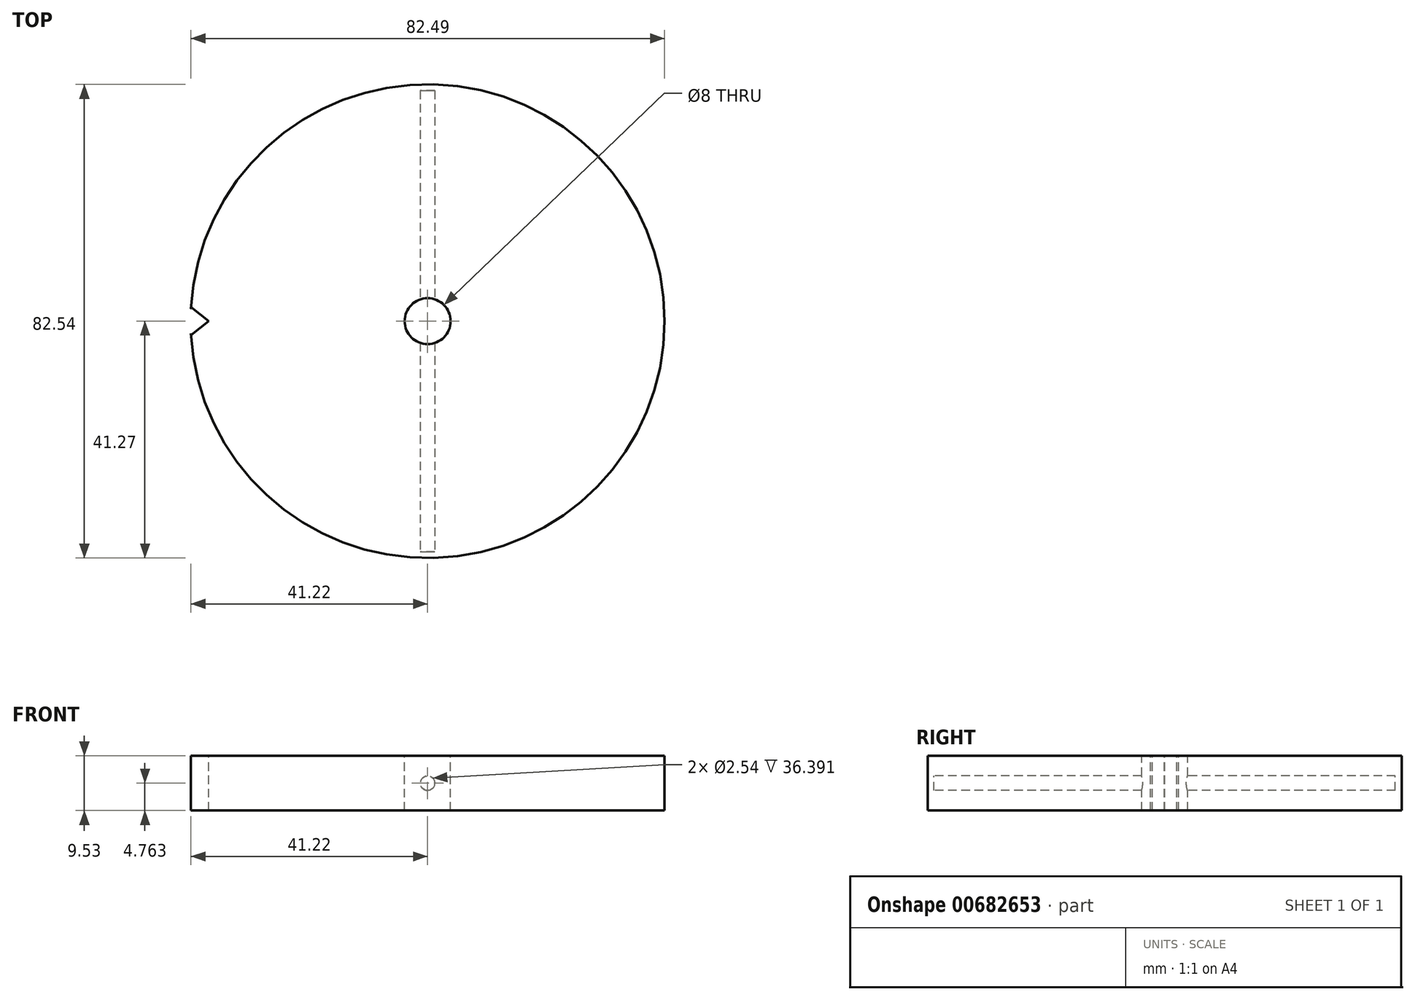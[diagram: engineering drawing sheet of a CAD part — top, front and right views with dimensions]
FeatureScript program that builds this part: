
annotation { "Feature Type Name" : "Feature", "Feature Type Description" : "" }
export const myFeature = defineFeature(function(context is Context, id is Id, definition is map)
    precondition{}
    {
        {
            var Q0;
            Q0=qCreatedBy(makeId("Top.planeOp"),FACE);
            var sketch = newSketch(context, id + "F0", { "sketchPlane" : qUnion([Q0])});
            skCircle(sketch, "E0", {"center": v(0, 0) * mm, "radius": 41.27 * mm});
            skSolve(sketch);
        }
        {
            var Q0;
            Q0 = qSketchRegion(id + "F0", true);
            extrude(context, id + "F1", {"entities" : qUnion([Q0]), "depth" : 9.52 * mm, "offsetDistance" : 25.4 * mm});
        }
        {
            var Q0;
            Q0=makeQuery(id+"F1.opExtrude","CAP_FACE",FACE,{"disambiguationData":[OSD([sQuery(id+"F0.wireOp",EDGE,"E0")])],"isStart":false});
            var sketch = newSketch(context, id + "F2", { "sketchPlane" : qUnion([Q0])});
            skCircle(sketch, "E1", {"center": v(0, 0) * mm, "radius": 38.1 * mm});
            skArc(sketch, "E2", {"start": v(3.17, 41.15) * mm, "mid": v(0, 38.1) * mm, "end": v(-3.17, 41.15) * mm});
            skLineSegment(sketch, "E3", {"start": v(-38.08, 0) * mm, "end": v(-41.19, 2.42) * mm});
            skLineSegment(sketch, "E4.MirrorCS", {"start": v(-38.08, 0) * mm, "end": v(-41.19, -2.42) * mm});
            skArc(sketch, "E5", {"start": v(-41.19, 2.42) * mm, "mid": v(-41.34, 0) * mm, "end": v(-41.19, -2.42) * mm});
            skSolve(sketch);
        }
        {
            var Q0;
            {var subQ1=sQuery(id+"F2.wireOp",EDGE,"E3");var subQ7=sQuery(id+"F2.wireOp",EDGE,"E1");var subQ9=makeQuery(id+"F2.imprint","INTERSECT",VERTEX,{"derivedFrom":[subQ7,subQ1]});Q0=makeQuery(id+"F2.imprint","IMPRINT",FACE,{"disambiguationData":[TD([[makeQuery(id+"F2.imprint","IMPRINT",EDGE,{"disambiguationData":[TD([[subQ9,-1.0]])],"derivedFrom":subQ7}),-1.0]])]});}
            var Q1;
            Q1=sQuery(id+"F2.wireOp",EDGE,"E3");
            var Q2;
            Q2=sQuery(id+"F2.wireOp",EDGE,"E4.MirrorCS");
            extrude(context, id + "F3", {"entities" : qUnion([Q0]), "operationType" : NewBodyOperationType.REMOVE, "flatOperationType" : FlatOperationType.REMOVE, "surfaceEntities" : qUnion([Q1, Q2]), "oppositeDirection" : true, "depth" : 25.4 * mm, "offsetDistance" : 25.4 * mm, "domain" : OperationDomain.MODEL});
        }
        {
            var Q0;
            {var subQ0=sQuery(id+"F2.wireOp",EDGE,"E1");var subQ180=makeQuery(id+"F3.boolean.opBoolean","COPY",FACE,{"derivedFrom":makeQuery(id+"F3.opExtrude","SWEPT_FACE",FACE,{"disambiguationData":[OSD([subQ0])]})});var subQ327=sQuery(id+"F0.wireOp",EDGE,"E0");Q0=makeQuery(id+"FR4VeuBJqVnm1tW_1.55.F3.boolean.opBoolean","SPLIT",FACE,{"disambiguationData":[TD([subQ180])],"derivedFrom":makeQuery(id+"FR4VeuBJqVnm1tW_1.54.F3.boolean.opBoolean","SPLIT",FACE,{"disambiguationData":[TD([subQ180])],"derivedFrom":makeQuery(id+"FR4VeuBJqVnm1tW_1.53.F3.boolean.opBoolean","SPLIT",FACE,{"disambiguationData":[TD([subQ180])],"derivedFrom":makeQuery(id+"FR4VeuBJqVnm1tW_1.52.F3.boolean.opBoolean","SPLIT",FACE,{"disambiguationData":[TD([subQ180])],"derivedFrom":makeQuery(id+"FR4VeuBJqVnm1tW_1.51.F3.boolean.opBoolean","SPLIT",FACE,{"disambiguationData":[TD([subQ180])],"derivedFrom":makeQuery(id+"FR4VeuBJqVnm1tW_1.50.F3.boolean.opBoolean","SPLIT",FACE,{"disambiguationData":[TD([subQ180])],"derivedFrom":makeQuery(id+"FR4VeuBJqVnm1tW_1.49.F3.boolean.opBoolean","SPLIT",FACE,{"disambiguationData":[TD([subQ180])],"derivedFrom":makeQuery(id+"FR4VeuBJqVnm1tW_1.48.F3.boolean.opBoolean","SPLIT",FACE,{"disambiguationData":[TD([subQ180])],"derivedFrom":makeQuery(id+"FR4VeuBJqVnm1tW_1.47.F3.boolean.opBoolean","SPLIT",FACE,{"disambiguationData":[TD([subQ180])],"derivedFrom":makeQuery(id+"FR4VeuBJqVnm1tW_1.46.F3.boolean.opBoolean","SPLIT",FACE,{"disambiguationData":[TD([subQ180])],"derivedFrom":makeQuery(id+"FR4VeuBJqVnm1tW_1.45.F3.boolean.opBoolean","SPLIT",FACE,{"disambiguationData":[TD([subQ180])],"derivedFrom":makeQuery(id+"FR4VeuBJqVnm1tW_1.44.F3.boolean.opBoolean","SPLIT",FACE,{"disambiguationData":[TD([subQ180])],"derivedFrom":makeQuery(id+"FR4VeuBJqVnm1tW_1.43.F3.boolean.opBoolean","SPLIT",FACE,{"disambiguationData":[TD([subQ180])],"derivedFrom":makeQuery(id+"FR4VeuBJqVnm1tW_1.42.F3.boolean.opBoolean","SPLIT",FACE,{"disambiguationData":[TD([subQ180])],"derivedFrom":makeQuery(id+"FR4VeuBJqVnm1tW_1.41.F3.boolean.opBoolean","SPLIT",FACE,{"disambiguationData":[TD([subQ180])],"derivedFrom":makeQuery(id+"FR4VeuBJqVnm1tW_1.40.F3.boolean.opBoolean","SPLIT",FACE,{"disambiguationData":[TD([subQ180])],"derivedFrom":makeQuery(id+"FR4VeuBJqVnm1tW_1.39.F3.boolean.opBoolean","SPLIT",FACE,{"disambiguationData":[TD([subQ180])],"derivedFrom":makeQuery(id+"FR4VeuBJqVnm1tW_1.38.F3.boolean.opBoolean","SPLIT",FACE,{"disambiguationData":[TD([subQ180])],"derivedFrom":makeQuery(id+"FR4VeuBJqVnm1tW_1.37.F3.boolean.opBoolean","SPLIT",FACE,{"disambiguationData":[TD([subQ180])],"derivedFrom":makeQuery(id+"FR4VeuBJqVnm1tW_1.36.F3.boolean.opBoolean","SPLIT",FACE,{"disambiguationData":[TD([subQ180])],"derivedFrom":makeQuery(id+"FR4VeuBJqVnm1tW_1.35.F3.boolean.opBoolean","SPLIT",FACE,{"disambiguationData":[TD([subQ180])],"derivedFrom":makeQuery(id+"FR4VeuBJqVnm1tW_1.34.F3.boolean.opBoolean","SPLIT",FACE,{"disambiguationData":[TD([subQ180])],"derivedFrom":makeQuery(id+"FR4VeuBJqVnm1tW_1.33.F3.boolean.opBoolean","SPLIT",FACE,{"disambiguationData":[TD([subQ180])],"derivedFrom":makeQuery(id+"FR4VeuBJqVnm1tW_1.32.F3.boolean.opBoolean","SPLIT",FACE,{"disambiguationData":[TD([subQ180])],"derivedFrom":makeQuery(id+"FR4VeuBJqVnm1tW_1.31.F3.boolean.opBoolean","SPLIT",FACE,{"disambiguationData":[TD([subQ180])],"derivedFrom":makeQuery(id+"FR4VeuBJqVnm1tW_1.30.F3.boolean.opBoolean","SPLIT",FACE,{"disambiguationData":[TD([subQ180])],"derivedFrom":makeQuery(id+"FR4VeuBJqVnm1tW_1.29.F3.boolean.opBoolean","SPLIT",FACE,{"disambiguationData":[TD([subQ180])],"derivedFrom":makeQuery(id+"FR4VeuBJqVnm1tW_1.28.F3.boolean.opBoolean","SPLIT",FACE,{"disambiguationData":[TD([subQ180])],"derivedFrom":makeQuery(id+"FR4VeuBJqVnm1tW_1.27.F3.boolean.opBoolean","SPLIT",FACE,{"disambiguationData":[TD([subQ180])],"derivedFrom":makeQuery(id+"FR4VeuBJqVnm1tW_1.26.F3.boolean.opBoolean","SPLIT",FACE,{"disambiguationData":[TD([subQ180])],"derivedFrom":makeQuery(id+"FR4VeuBJqVnm1tW_1.25.F3.boolean.opBoolean","SPLIT",FACE,{"disambiguationData":[TD([subQ180])],"derivedFrom":makeQuery(id+"FR4VeuBJqVnm1tW_1.24.F3.boolean.opBoolean","SPLIT",FACE,{"disambiguationData":[TD([subQ180])],"derivedFrom":makeQuery(id+"FR4VeuBJqVnm1tW_1.23.F3.boolean.opBoolean","SPLIT",FACE,{"disambiguationData":[TD([subQ180])],"derivedFrom":makeQuery(id+"FR4VeuBJqVnm1tW_1.22.F3.boolean.opBoolean","SPLIT",FACE,{"disambiguationData":[TD([subQ180])],"derivedFrom":makeQuery(id+"FR4VeuBJqVnm1tW_1.21.F3.boolean.opBoolean","SPLIT",FACE,{"disambiguationData":[TD([subQ180])],"derivedFrom":makeQuery(id+"FR4VeuBJqVnm1tW_1.20.F3.boolean.opBoolean","SPLIT",FACE,{"disambiguationData":[TD([subQ180])],"derivedFrom":makeQuery(id+"FR4VeuBJqVnm1tW_1.19.F3.boolean.opBoolean","SPLIT",FACE,{"disambiguationData":[TD([subQ180])],"derivedFrom":makeQuery(id+"FR4VeuBJqVnm1tW_1.18.F3.boolean.opBoolean","SPLIT",FACE,{"disambiguationData":[TD([subQ180])],"derivedFrom":makeQuery(id+"FR4VeuBJqVnm1tW_1.17.F3.boolean.opBoolean","SPLIT",FACE,{"disambiguationData":[TD([subQ180])],"derivedFrom":makeQuery(id+"FR4VeuBJqVnm1tW_1.16.F3.boolean.opBoolean","SPLIT",FACE,{"disambiguationData":[TD([subQ180])],"derivedFrom":makeQuery(id+"FR4VeuBJqVnm1tW_1.15.F3.boolean.opBoolean","SPLIT",FACE,{"disambiguationData":[TD([subQ180])],"derivedFrom":makeQuery(id+"FR4VeuBJqVnm1tW_1.14.F3.boolean.opBoolean","SPLIT",FACE,{"disambiguationData":[TD([subQ180])],"derivedFrom":makeQuery(id+"FR4VeuBJqVnm1tW_1.13.F3.boolean.opBoolean","SPLIT",FACE,{"disambiguationData":[TD([subQ180])],"derivedFrom":makeQuery(id+"FR4VeuBJqVnm1tW_1.12.F3.boolean.opBoolean","SPLIT",FACE,{"disambiguationData":[TD([subQ180])],"derivedFrom":makeQuery(id+"FR4VeuBJqVnm1tW_1.11.F3.boolean.opBoolean","SPLIT",FACE,{"disambiguationData":[TD([subQ180])],"derivedFrom":makeQuery(id+"FR4VeuBJqVnm1tW_1.10.F3.boolean.opBoolean","SPLIT",FACE,{"disambiguationData":[TD([subQ180])],"derivedFrom":makeQuery(id+"FR4VeuBJqVnm1tW_1.9.F3.boolean.opBoolean","SPLIT",FACE,{"disambiguationData":[TD([subQ180])],"derivedFrom":makeQuery(id+"FR4VeuBJqVnm1tW_1.8.F3.boolean.opBoolean","SPLIT",FACE,{"disambiguationData":[TD([subQ180])],"derivedFrom":makeQuery(id+"FR4VeuBJqVnm1tW_1.7.F3.boolean.opBoolean","SPLIT",FACE,{"disambiguationData":[TD([subQ180])],"derivedFrom":makeQuery(id+"FR4VeuBJqVnm1tW_1.6.F3.boolean.opBoolean","SPLIT",FACE,{"disambiguationData":[TD([subQ180])],"derivedFrom":makeQuery(id+"FR4VeuBJqVnm1tW_1.5.F3.boolean.opBoolean","SPLIT",FACE,{"disambiguationData":[TD([subQ180])],"derivedFrom":makeQuery(id+"FR4VeuBJqVnm1tW_1.4.F3.boolean.opBoolean","SPLIT",FACE,{"disambiguationData":[TD([subQ180])],"derivedFrom":makeQuery(id+"FR4VeuBJqVnm1tW_1.3.F3.boolean.opBoolean","SPLIT",FACE,{"disambiguationData":[TD([subQ180])],"derivedFrom":makeQuery(id+"FR4VeuBJqVnm1tW_1.2.F3.boolean.opBoolean","SPLIT",FACE,{"disambiguationData":[TD([subQ180])],"derivedFrom":makeQuery(id+"FR4VeuBJqVnm1tW_1.1.F3.boolean.opBoolean","SPLIT",FACE,{"disambiguationData":[TD([subQ180])],"derivedFrom":makeQuery(id+"F1.opExtrude","CAP_FACE",FACE,{"disambiguationData":[OSD([subQ327])],"isStart":false})})})})})})})})})})})})})})})})})})})})})})})})})})})})})})})})})})})})})})})})})})})})})})})})})})})})})})})});}
            var sketch = newSketch(context, id + "F4", { "sketchPlane" : qUnion([Q0])});
            skCircle(sketch, "E6", {"center": v(0, 0) * mm, "radius": 4 * mm});
            skSolve(sketch);
        }
        {
            var Q0;
            Q0 = qSketchRegion(id + "F4", true);
            extrude(context, id + "F5", {"entities" : qUnion([Q0]), "operationType" : NewBodyOperationType.REMOVE, "flatOperationType" : FlatOperationType.REMOVE, "oppositeDirection" : true, "depth" : 25.4 * mm, "offsetDistance" : 25.4 * mm, "domain" : OperationDomain.MODEL});
        }
        {
            var Q0;
            Q0=qCreatedBy(makeId("Front.planeOp"),FACE);
            var sketch = newSketch(context, id + "F6", { "sketchPlane" : qUnion([Q0])});
            skLineSegment(sketch, "E7", {"start": v(0, 0) * mm, "end": v(0, 4.76) * mm});
            skCircle(sketch, "E8", {"center": v(0, 4.76) * mm, "radius": 1.27 * mm});
            skSolve(sketch);
        }
        {
            var Q0;
            Q0=makeQuery(id+"F6.imprint","IMPRINT",FACE,{"disambiguationData":[TD([[makeQuery(id+"F6.imprint","IMPRINT",EDGE,{"derivedFrom":sQuery(id+"F6.wireOp",EDGE,"E8")}),1.0]])]});
            extrude(context, id + "F7", {"entities" : qUnion([Q0]), "operationType" : NewBodyOperationType.REMOVE, "endBound" : BoundingType.SYMMETRIC, "oppositeDirection" : true, "depth" : 80.37 * mm, "offsetDistance" : 25.4 * mm});
        }
    });
